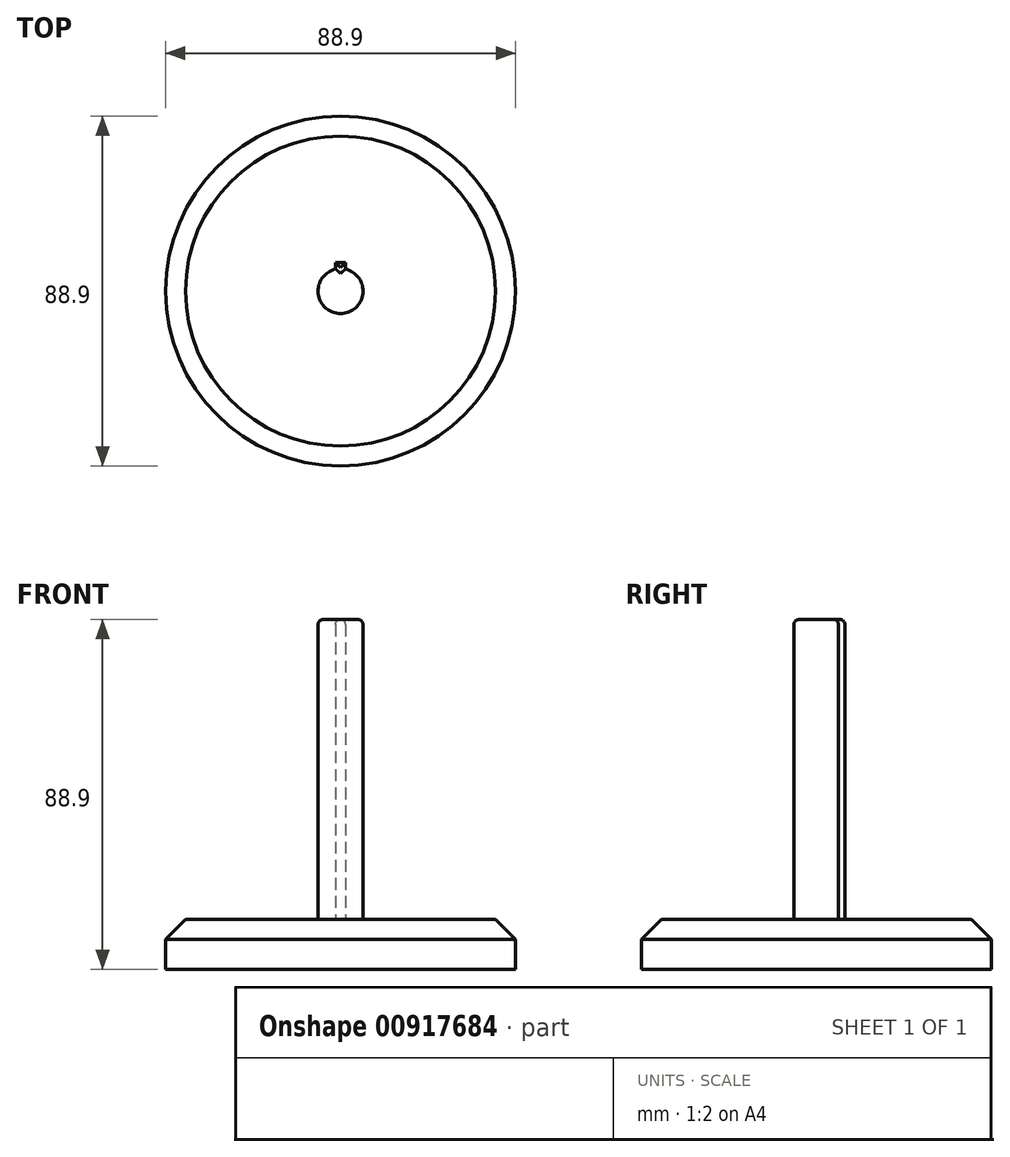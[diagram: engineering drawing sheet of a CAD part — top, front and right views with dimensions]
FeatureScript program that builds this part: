
annotation { "Feature Type Name" : "Feature", "Feature Type Description" : "" }
export const myFeature = defineFeature(function(context is Context, id is Id, definition is map)
    precondition{}
    {
        {
            var Q0;
            Q0=qCreatedBy(makeId("Top.planeOp"),FACE);
            var sketch = newSketch(context, id + "F0", { "sketchPlane" : qUnion([Q0])});
            skCircle(sketch, "E0", {"center": v(0, 0) * mm, "radius": 44.45 * mm});
            skArc(sketch, "E1", {"start": v(-1.27, 5.57) * mm, "mid": v(0, -5.72) * mm, "end": v(1.27, 5.57) * mm});
            skLineSegment(sketch, "E2.bottom", {"start": v(-1.27, 7.24) * mm, "end": v(1.27, 7.24) * mm});
            skLineSegment(sketch, "E2.left", {"start": v(-1.27, 7.24) * mm, "end": v(-1.27, 5.57) * mm});
            skLineSegment(sketch, "E2.right", {"start": v(1.27, 7.24) * mm, "end": v(1.27, 5.57) * mm});
            skPoint(sketch, "E2.middle", {"position": v(0, 5.56) * mm});
            skPoint(sketch, "E3.orphan", {"position": v(-1.27, 3.88) * mm});
            skPoint(sketch, "E4.orphan", {"position": v(1.27, 3.88) * mm});
            skSolve(sketch);
        }
        {
            var Q0;
            Q0=makeQuery(id+"F0.imprint","IMPRINT",FACE,{"disambiguationData":[TD([[makeQuery(id+"F0.imprint","IMPRINT",EDGE,{"derivedFrom":sQuery(id+"F0.wireOp",EDGE,"E0")}),1.0]])]});
            extrude(context, id + "F1", {"entities" : qUnion([Q0]), "depth" : 12.7 * mm, "offsetDistance" : 25.4 * mm});
        }
        {
            var Q0;
            Q0=makeQuery(id+"F0.imprint","IMPRINT",FACE,{"disambiguationData":[TD([[makeQuery(id+"F0.imprint","IMPRINT",EDGE,{"derivedFrom":sQuery(id+"F0.wireOp",EDGE,"E1")}),1.0]])]});
            extrude(context, id + "F2", {"entities" : qUnion([Q0]), "operationType" : NewBodyOperationType.ADD, "depth" : 88.9 * mm, "offsetDistance" : 25.4 * mm});
        }
        {
            var Q0;
            Q0=makeQuery(id+"F2.opExtrude","CAP_FACE",FACE,{"disambiguationData":[OSD([sQuery(id+"F0.wireOp",EDGE,"E1"),sQuery(id+"F0.wireOp",EDGE,"E2.bottom"),sQuery(id+"F0.wireOp",EDGE,"E2.left"),sQuery(id+"F0.wireOp",EDGE,"E2.right")])],"isStart":false});
            fillet(context, id + "F3", {"entities" : qUnion([Q0]), "radius" : 1.27 * mm, "tangentPropagation" : true, "allowEdgeOverflow" : false});
        }
        {
            var Q0;
            Q0=makeQuery(id+"F1.opExtrude","CAP_EDGE",EDGE,{"disambiguationData":[OSD([sQuery(id+"F0.wireOp",EDGE,"E0")])],"isStart":false});
            chamfer(context, id + "F4", {"entities" : qUnion([Q0]), "width" : 5.08 * mm, "tangentPropagation" : true});
        }
    });
